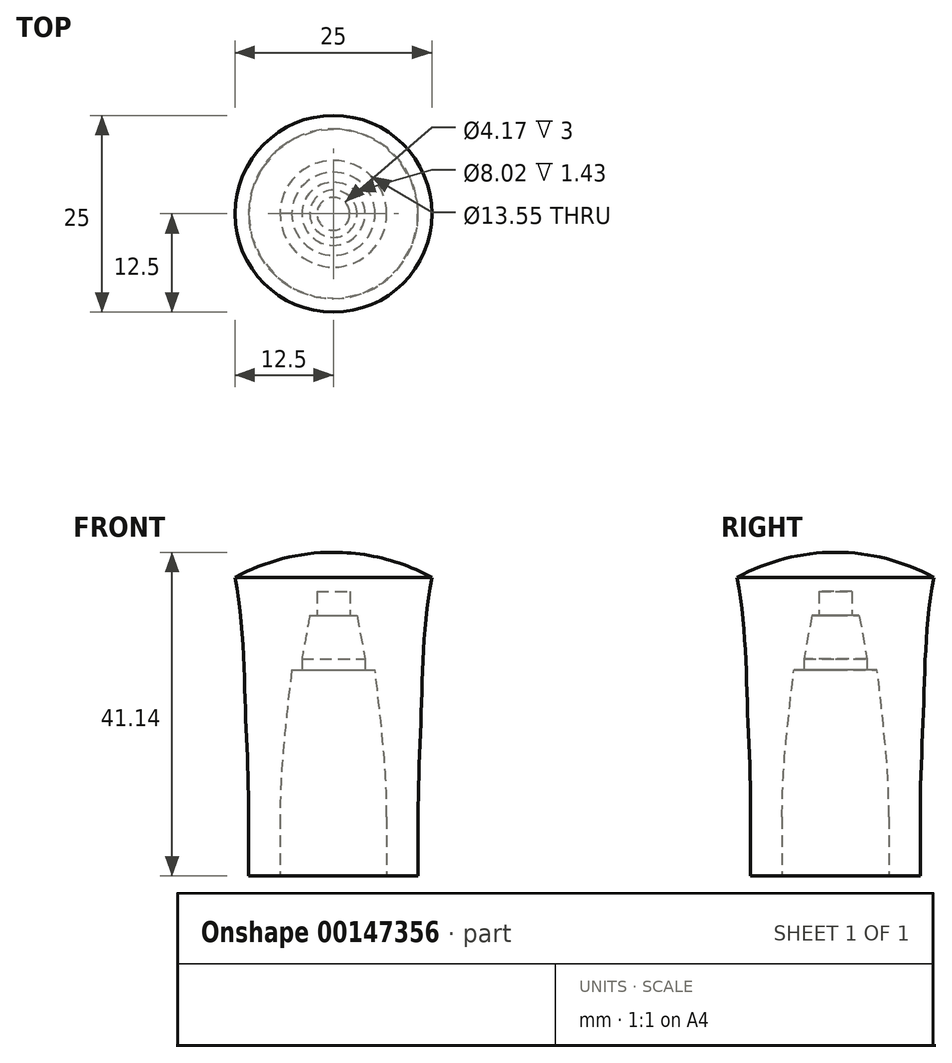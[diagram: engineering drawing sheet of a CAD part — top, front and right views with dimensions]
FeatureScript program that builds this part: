
annotation { "Feature Type Name" : "Feature", "Feature Type Description" : "" }
export const myFeature = defineFeature(function(context is Context, id is Id, definition is map)
    precondition{}
    {
        {
            var Q0;
            Q0=qCreatedBy(makeId("Front.planeOp"),FACE);
            var sketch = newSketch(context, id + "F0", { "sketchPlane" : qUnion([Q0])});
            skLineSegment(sketch, "E0", {"start": v(6.78, 0) * mm, "end": v(6.78, 7.5) * mm});
            skLineSegment(sketch, "E1", {"start": v(0, 36.14) * mm, "end": v(2.08, 36.14) * mm});
            skLineSegment(sketch, "E2", {"start": v(2.08, 36.14) * mm, "end": v(2.08, 33.14) * mm});
            skLineSegment(sketch, "E3", {"start": v(2.08, 33.14) * mm, "end": v(3, 33.14) * mm});
            skLineSegment(sketch, "E4", {"start": v(3, 33.14) * mm, "end": v(4, 27.6) * mm});
            skLineSegment(sketch, "E5", {"start": v(4, 27.6) * mm, "end": v(4, 26.18) * mm});
            skLineSegment(sketch, "E6", {"start": v(4, 26.18) * mm, "end": v(5.29, 26.18) * mm});
            skPoint(sketch, "E7", {"position": v(6.29, 17.02) * mm});
            skFitSpline(sketch, "E8", {"points": [v(5.29, 26.18) * mm, v(6.29, 17.02) * mm, v(6.78, 7.5) * mm], "startDerivative": vector(2.28, -18.37) * mm, "endDerivative": vector(0, -22.3) * mm});
            skLineSegment(sketch, "E9", {"start": v(6.78, 0) * mm, "end": v(10.78, 0) * mm});
            skLineSegment(sketch, "E10", {"start": v(10.78, 0) * mm, "end": v(10.78, 7.5) * mm});
            skFitSpline(sketch, "E11", {"points": [v(10.78, 7.5) * mm, v(11.17, 21.02) * mm, v(12.5, 37.93) * mm], "startDerivative": vector(-0.1, 32.95) * mm, "endDerivative": vector(6.22, 31.93) * mm});
            skArc(sketch, "E12", {"start": v(12.5, 37.93) * mm, "mid": v(6.45, 40.32) * mm, "end": v(0, 41.14) * mm});
            skLineSegment(sketch, "E13", {"start": v(0, 36.14) * mm, "end": v(0, 41.14) * mm});
            skSolve(sketch);
        }
        {
            var Q0;
            Q0=makeQuery(id+"F0.imprint","IMPRINT",FACE,{"disambiguationData":[TD([[makeQuery(id+"F0.imprint","IMPRINT",EDGE,{"derivedFrom":sQuery(id+"F0.wireOp",EDGE,"E0")}),-1.0]])]});
            var Q1;
            Q1=sQuery(id+"F0.wireOp",EDGE,"E13");
            revolve(context, id + "F1", {"entities" : qUnion([Q0]), "axis" : qUnion([Q1]), "revolveType" : RevolveType.FULL});
        }
    });
